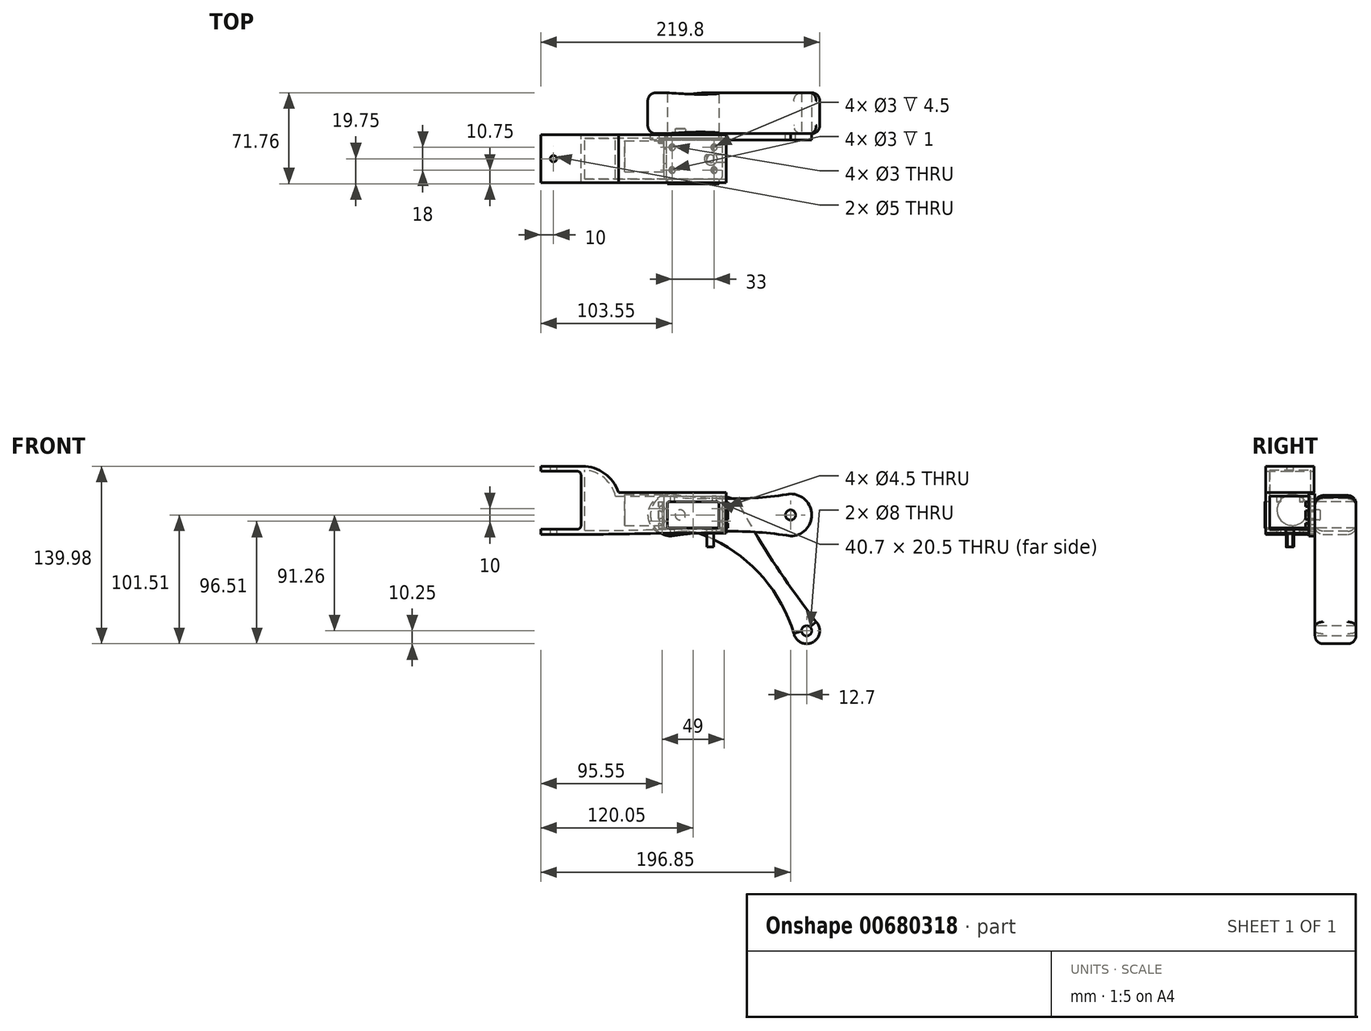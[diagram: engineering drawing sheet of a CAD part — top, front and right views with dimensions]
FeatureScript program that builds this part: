
annotation { "Feature Type Name" : "Feature", "Feature Type Description" : "" }
export const myFeature = defineFeature(function(context is Context, id is Id, definition is map)
    precondition{}
    {
        {
            var Q0;
            Q0=qCreatedBy(makeId("Top.planeOp"),FACE);
            var sketch = newSketch(context, id + "F0", { "sketchPlane" : qUnion([Q0])});
            skLineSegment(sketch, "E0.bottom", {"start": v(-20.35, 19.75) * mm, "end": v(20.35, 19.75) * mm});
            skLineSegment(sketch, "E0.top", {"start": v(-20.35, -19.75) * mm, "end": v(20.35, -19.75) * mm});
            skLineSegment(sketch, "E0.left", {"start": v(-20.35, 19.75) * mm, "end": v(-20.35, -19.75) * mm});
            skLineSegment(sketch, "E0.right", {"start": v(20.35, 19.75) * mm, "end": v(20.35, -19.75) * mm});
            skPoint(sketch, "E1", {"position": v(-20.35, 0) * mm});
            skPoint(sketch, "E2", {"position": v(0, 19.75) * mm});
            skLineSegment(sketch, "E3.bottom", {"start": v(-27.25, 14.75) * mm, "end": v(27.25, 14.75) * mm});
            skLineSegment(sketch, "E3.top", {"start": v(-27.25, 12.25) * mm, "end": v(27.25, 12.25) * mm});
            skLineSegment(sketch, "E3.left", {"start": v(-27.25, 14.75) * mm, "end": v(-27.25, 12.25) * mm});
            skLineSegment(sketch, "E3.right", {"start": v(27.25, 14.75) * mm, "end": v(27.25, 12.25) * mm});
            skPoint(sketch, "E4", {"position": v(0, 14.75) * mm});
            skSolve(sketch);
        }
        {
            var Q0;
            Q0 = qSketchRegion(id + "F0", true);
            extrude(context, id + "F1", {"entities" : qUnion([Q0]), "depth" : 20.5 * mm, "offsetDistance" : 25.4 * mm});
        }
        {
            var Q0;
            Q0=makeQuery(id+"F1.opExtrude","SWEPT_FACE",FACE,{"disambiguationData":[OSD([sQuery(id+"F0.wireOp",EDGE,"E0.bottom")])]});
            var sketch = newSketch(context, id + "F2", { "sketchPlane" : qUnion([Q0])});
            skCircle(sketch, "E5", {"center": v(10.1, 10.25) * mm, "radius": 10.25 * mm, "construction": true});
            skLineSegment(sketch, "E6", {"start": v(20.35, 10.25) * mm, "end": v(-20.35, 10.25) * mm, "construction": true});
            skCircle(sketch, "E7", {"center": v(10.1, 10.25) * mm, "radius": 4 * mm});
            skSolve(sketch);
        }
        {
            var Q0;
            Q0 = qSketchRegion(id + "F2", true);
            extrude(context, id + "F3", {"entities" : qUnion([Q0]), "operationType" : NewBodyOperationType.ADD, "depth" : 4 * mm, "offsetDistance" : 25.4 * mm});
        }
        {
            var Q0;
            Q0=makeQuery(id+"F3.opExtrude","CAP_EDGE",EDGE,{"disambiguationData":[OSD([sQuery(id+"F2.wireOp",EDGE,"E7")])],"isStart":false});
            fillet(context, id + "F4", {"entities" : qUnion([Q0]), "radius" : .5 * mm, "tangentPropagation" : true, "allowEdgeOverflow" : false});
        }
        {
            var Q0;
            {var subQ0=sQuery(id+"F0.wireOp",EDGE,"E3.bottom");Q0=makeQuery(id+"F1.opExtrude","SWEPT_FACE",FACE,{"disambiguationData":[OSD([subQ0]),TDD([makeQuery(id+"F0.imprint","IMPRINT",EDGE,{"disambiguationData":[TD([[makeQuery(id+"F0.imprint","INTERSECT",VERTEX,{"derivedFrom":[subQ0,sQuery(id+"F0.wireOp",EDGE,"E3.left")]}),-1.0]])],"derivedFrom":subQ0})])]});}
            var sketch = newSketch(context, id + "F5", { "sketchPlane" : qUnion([Q0])});
            skLineSegment(sketch, "E8", {"start": v(27.25, 10.25) * mm, "end": v(20.35, 10.25) * mm, "construction": true});
            skLineSegment(sketch, "E9", {"start": v(24.5, 0) * mm, "end": v(24.5, 20.5) * mm, "construction": true});
            skCircle(sketch, "E10", {"center": v(24.5, 15.25) * mm, "radius": 2.25 * mm, "construction": true});
            skArc(sketch, "E11.MirrorC", {"start": v(26.18, 3.75) * mm, "mid": v(22.25, 5.25) * mm, "end": v(26.18, 6.75) * mm});
            skLineSegment(sketch, "E12.bottom", {"start": v(27.25, 3.75) * mm, "end": v(26.18, 3.75) * mm});
            skLineSegment(sketch, "E12.top", {"start": v(27.25, 6.75) * mm, "end": v(26.18, 6.75) * mm});
            skLineSegment(sketch, "E12.left", {"start": v(27.25, 3.75) * mm, "end": v(27.25, 6.75) * mm});
            skLineSegment(sketch, "E13", {"start": v(24.5, 5.25) * mm, "end": v(29.17, 5.25) * mm, "construction": true});
            skPoint(sketch, "E14", {"position": v(27.25, 5.25) * mm});
            skLineSegment(sketch, "E15.MirrorCS", {"start": v(27.25, 16.75) * mm, "end": v(26.18, 16.75) * mm});
            skLineSegment(sketch, "E16.MirrorCS", {"start": v(27.25, 13.75) * mm, "end": v(26.18, 13.75) * mm});
            skLineSegment(sketch, "E17.MirrorCS", {"start": v(27.25, 16.75) * mm, "end": v(27.25, 13.75) * mm});
            skArc(sketch, "E18.MirrorCS", {"start": v(26.18, 16.75) * mm, "mid": v(22.25, 15.25) * mm, "end": v(26.18, 13.75) * mm});
            skPoint(sketch, "E19.MirrorP", {"position": v(27.25, 15.25) * mm});
            skLineSegment(sketch, "E20.MirrorCS", {"start": v(-27.25, 13.75) * mm, "end": v(-26.18, 13.75) * mm});
            skLineSegment(sketch, "E21.MirrorCS", {"start": v(-27.25, 3.75) * mm, "end": v(-26.18, 3.75) * mm});
            skLineSegment(sketch, "E22.MirrorCS", {"start": v(-27.25, 6.75) * mm, "end": v(-26.18, 6.75) * mm});
            skLineSegment(sketch, "E23.MirrorCS", {"start": v(-27.25, 16.75) * mm, "end": v(-26.18, 16.75) * mm});
            skLineSegment(sketch, "E24.MirrorCS", {"start": v(-27.25, 3.75) * mm, "end": v(-27.25, 6.75) * mm});
            skLineSegment(sketch, "E25.MirrorCS", {"start": v(-27.25, 16.75) * mm, "end": v(-27.25, 13.75) * mm});
            skPoint(sketch, "E26.MirrorP", {"position": v(-27.25, 5.25) * mm});
            skArc(sketch, "E27.MirrorCS", {"start": v(-26.18, 3.75) * mm, "mid": v(-22.25, 5.25) * mm, "end": v(-26.18, 6.75) * mm});
            skArc(sketch, "E28.MirrorCS", {"start": v(-26.18, 16.75) * mm, "mid": v(-22.25, 15.25) * mm, "end": v(-26.18, 13.75) * mm});
            skCircle(sketch, "E29.MirrorC", {"center": v(-24.5, 15.25) * mm, "radius": 2.25 * mm, "construction": true});
            skPoint(sketch, "E30.MirrorP", {"position": v(-27.25, 15.25) * mm});
            skSolve(sketch);
        }
        {
            var Q0;
            Q0 = qSketchRegion(id + "F5", true);
            var Q1;
            {var subQ0=sQuery(id+"F0.wireOp",EDGE,"E3.top");Q1=makeQuery(id+"F1.opExtrude","SWEPT_FACE",FACE,{"disambiguationData":[OSD([subQ0]),TDD([makeQuery(id+"F0.imprint","IMPRINT",EDGE,{"disambiguationData":[TD([[makeQuery(id+"F0.imprint","INTERSECT",VERTEX,{"derivedFrom":[subQ0,sQuery(id+"F0.wireOp",EDGE,"E3.left")]}),-1.0]])],"derivedFrom":subQ0})])]});}
            extrude(context, id + "F6", {"entities" : qUnion([Q0]), "operationType" : NewBodyOperationType.REMOVE, "endBound" : BoundingType.UP_TO_SURFACE, "oppositeDirection" : true, "depth" : 25.4 * mm, "endBoundEntityFace" : qUnion([Q1]), "offsetDistance" : 25.4 * mm});
        }
        {
            var Q0;
            {var subQ0=sQuery(id+"F0.wireOp",EDGE,"E0.right");Q0=makeQuery(id+"F1.opExtrude","CAP_EDGE",EDGE,{"disambiguationData":[OSD([subQ0]),TDD([makeQuery(id+"F0.imprint","IMPRINT",EDGE,{"disambiguationData":[TD([[makeQuery(id+"F0.imprint","INTERSECT",VERTEX,{"derivedFrom":[sQuery(id+"F0.wireOp",EDGE,"E0.top"),subQ0]}),1.0]])],"derivedFrom":subQ0})])],"isStart":true});}
            var Q1;
            {var subQ0=sQuery(id+"F0.wireOp",EDGE,"E0.right");Q1=makeQuery(id+"F1.opExtrude","CAP_EDGE",EDGE,{"disambiguationData":[OSD([subQ0]),TDD([makeQuery(id+"F0.imprint","IMPRINT",EDGE,{"disambiguationData":[TD([[makeQuery(id+"F0.imprint","INTERSECT",VERTEX,{"derivedFrom":[sQuery(id+"F0.wireOp",EDGE,"E0.top"),subQ0]}),1.0]])],"derivedFrom":subQ0})])],"isStart":false});}
            var Q2;
            {var subQ0=sQuery(id+"F0.wireOp",EDGE,"E0.left");Q2=makeQuery(id+"F1.opExtrude","CAP_EDGE",EDGE,{"disambiguationData":[OSD([subQ0]),TDD([makeQuery(id+"F0.imprint","IMPRINT",EDGE,{"disambiguationData":[TD([[makeQuery(id+"F0.imprint","INTERSECT",VERTEX,{"derivedFrom":[sQuery(id+"F0.wireOp",EDGE,"E0.top"),subQ0]}),1.0]])],"derivedFrom":subQ0})])],"isStart":true});}
            var Q3;
            {var subQ0=sQuery(id+"F0.wireOp",EDGE,"E0.left");Q3=makeQuery(id+"F1.opExtrude","CAP_EDGE",EDGE,{"disambiguationData":[OSD([subQ0]),TDD([makeQuery(id+"F0.imprint","IMPRINT",EDGE,{"disambiguationData":[TD([[makeQuery(id+"F0.imprint","INTERSECT",VERTEX,{"derivedFrom":[sQuery(id+"F0.wireOp",EDGE,"E0.top"),subQ0]}),1.0]])],"derivedFrom":subQ0})])],"isStart":false});}
            var Q4;
            Q4=makeQuery(id+"F1.opExtrude","CAP_EDGE",EDGE,{"disambiguationData":[OSD([sQuery(id+"F0.wireOp",EDGE,"E0.bottom")])],"isStart":false});
            var Q5;
            Q5=makeQuery(id+"F1.opExtrude","SWEPT_EDGE",EDGE,{"disambiguationData":[OSD([sQuery(id+"F0.wireOp",EDGE,"E0.bottom"),sQuery(id+"F0.wireOp",EDGE,"E0.right")])]});
            var Q6;
            Q6=makeQuery(id+"F1.opExtrude","CAP_EDGE",EDGE,{"disambiguationData":[OSD([sQuery(id+"F0.wireOp",EDGE,"E0.bottom")])],"isStart":true});
            var Q7;
            {var subQ0=sQuery(id+"F0.wireOp",EDGE,"E0.right");Q7=makeQuery(id+"F1.opExtrude","CAP_EDGE",EDGE,{"disambiguationData":[OSD([subQ0]),TDD([makeQuery(id+"F0.imprint","IMPRINT",EDGE,{"disambiguationData":[TD([[makeQuery(id+"F0.imprint","INTERSECT",VERTEX,{"derivedFrom":[sQuery(id+"F0.wireOp",EDGE,"E0.bottom"),subQ0]}),-1.0]])],"derivedFrom":subQ0})])],"isStart":true});}
            var Q8;
            {var subQ0=sQuery(id+"F0.wireOp",EDGE,"E0.right");Q8=makeQuery(id+"F1.opExtrude","CAP_EDGE",EDGE,{"disambiguationData":[OSD([subQ0]),TDD([makeQuery(id+"F0.imprint","IMPRINT",EDGE,{"disambiguationData":[TD([[makeQuery(id+"F0.imprint","INTERSECT",VERTEX,{"derivedFrom":[sQuery(id+"F0.wireOp",EDGE,"E0.bottom"),subQ0]}),-1.0]])],"derivedFrom":subQ0})])],"isStart":false});}
            var Q9;
            Q9=makeQuery(id+"F1.opExtrude","SWEPT_EDGE",EDGE,{"disambiguationData":[OSD([sQuery(id+"F0.wireOp",EDGE,"E0.bottom"),sQuery(id+"F0.wireOp",EDGE,"E0.left")])]});
            var Q10;
            {var subQ0=sQuery(id+"F0.wireOp",EDGE,"E0.left");Q10=makeQuery(id+"F1.opExtrude","CAP_EDGE",EDGE,{"disambiguationData":[OSD([subQ0]),TDD([makeQuery(id+"F0.imprint","IMPRINT",EDGE,{"disambiguationData":[TD([[makeQuery(id+"F0.imprint","INTERSECT",VERTEX,{"derivedFrom":[sQuery(id+"F0.wireOp",EDGE,"E0.bottom"),subQ0]}),-1.0]])],"derivedFrom":subQ0})])],"isStart":true});}
            var Q11;
            {var subQ0=sQuery(id+"F0.wireOp",EDGE,"E0.left");Q11=makeQuery(id+"F1.opExtrude","CAP_EDGE",EDGE,{"disambiguationData":[OSD([subQ0]),TDD([makeQuery(id+"F0.imprint","IMPRINT",EDGE,{"disambiguationData":[TD([[makeQuery(id+"F0.imprint","INTERSECT",VERTEX,{"derivedFrom":[sQuery(id+"F0.wireOp",EDGE,"E0.bottom"),subQ0]}),-1.0]])],"derivedFrom":subQ0})])],"isStart":false});}
            fillet(context, id + "F7", {"entities" : qUnion([Q0, Q1, Q2, Q3, Q4, Q5, Q6, Q7, Q8, Q9, Q10, Q11]), "radius" : 1 * mm, "tangentPropagation" : true, "allowEdgeOverflow" : false});
        }
        {
            var Q0;
            Q0=makeQuery(id+"F1.opExtrude","SWEPT_FACE",FACE,{"disambiguationData":[OSD([sQuery(id+"F0.wireOp",EDGE,"E0.bottom")])]});
            var sketch = newSketch(context, id + "F8", { "sketchPlane" : qUnion([Q0])});
            skLineSegment(sketch, "E31.bottom", {"start": v(33.6, -6.35) * mm, "end": v(-93.4, -6.35) * mm, "construction": true});
            skLineSegment(sketch, "E31.top", {"start": v(33.6, 26.85) * mm, "end": v(-93.4, 26.85) * mm, "construction": true});
            skLineSegment(sketch, "E31.left", {"start": v(33.6, -6.35) * mm, "end": v(33.6, 26.85) * mm, "construction": true});
            skLineSegment(sketch, "E31.right", {"start": v(-93.4, -6.35) * mm, "end": v(-93.4, 26.85) * mm, "construction": true});
            skCircle(sketch, "E32", {"center": v(-76.8, 10.25) * mm, "radius": 16.6 * mm, "construction": true});
            skPoint(sketch, "E32.centerSnap0", {"position": v(-93.4, 10.25) * mm});
            skCircle(sketch, "E33", {"center": v(-46.9, 10.25) * mm, "radius": 13.3 * mm, "construction": true});
            skLineSegment(sketch, "E34", {"start": v(-93.4, 10.25) * mm, "end": v(33.6, 10.25) * mm, "construction": true});
            skArc(sketch, "E35", {"start": v(-76.8, 26.85) * mm, "mid": v(-93.4, 10.25) * mm, "end": v(-76.8, -6.35) * mm});
            skArc(sketch, "E36", {"start": v(17, -6.35) * mm, "mid": v(-29.9, -2.58) * mm, "end": v(-76.8, -6.35) * mm});
            skLineSegment(sketch, "E37", {"start": v(-29.9, 26.85) * mm, "end": v(-29.9, -6.35) * mm, "construction": true});
            skPoint(sketch, "E38.MirrorP", {"position": v(33.6, 10.25) * mm});
            skArc(sketch, "E39.MirrorCS", {"start": v(17, 26.85) * mm, "mid": v(33.6, 10.25) * mm, "end": v(17, -6.35) * mm});
            skArc(sketch, "E40.MirrorCS", {"start": v(17, 26.85) * mm, "mid": v(-29.9, 23.08) * mm, "end": v(-76.8, 26.85) * mm});
            skCircle(sketch, "E41", {"center": v(-76.8, 10.25) * mm, "radius": 4 * mm});
            skLineSegment(sketch, "E42.bottom", {"start": v(-20.35, 0) * mm, "end": v(20.35, 0) * mm});
            skLineSegment(sketch, "E42.top", {"start": v(-20.35, 20.5) * mm, "end": v(20.35, 20.5) * mm});
            skLineSegment(sketch, "E42.left", {"start": v(-20.35, 0) * mm, "end": v(-20.35, 20.5) * mm});
            skLineSegment(sketch, "E42.right", {"start": v(20.35, 0) * mm, "end": v(20.35, 20.5) * mm});
            skCircle(sketch, "E43", {"center": v(-24.5, 15.25) * mm, "radius": 2.25 * mm});
            skCircle(sketch, "E44.MirrorC", {"center": v(-24.5, 5.25) * mm, "radius": 2.25 * mm});
            skCircle(sketch, "E45.MirrorC", {"center": v(24.5, 5.25) * mm, "radius": 2.25 * mm});
            skCircle(sketch, "E46.MirrorC", {"center": v(24.5, 15.25) * mm, "radius": 2.25 * mm});
            skSolve(sketch);
        }
        {
            var Q0;
            Q0 = qSketchRegion(id + "F8", true);
            var Q1;
            {var subQ0=sQuery(id+"F0.wireOp",EDGE,"E3.bottom");Q1=makeQuery(id+"F1.opExtrude","SWEPT_FACE",FACE,{"disambiguationData":[OSD([subQ0]),TDD([makeQuery(id+"F0.imprint","IMPRINT",EDGE,{"disambiguationData":[TD([[makeQuery(id+"F0.imprint","INTERSECT",VERTEX,{"derivedFrom":[subQ0,sQuery(id+"F0.wireOp",EDGE,"E3.right")]}),1.0]])],"derivedFrom":subQ0})])]});}
            extrude(context, id + "F9", {"entities" : qUnion([Q0]), "endBound" : BoundingType.UP_TO_SURFACE, "oppositeDirection" : true, "depth" : 43.94 * mm, "endBoundEntityFace" : qUnion([Q1]), "offsetDistance" : 6.35 * mm, "offsetOppositeDirection" : true});
        }
        {
            var Q0;
            Q0=makeQuery(id+"F1.opExtrude","SWEPT_FACE",FACE,{"disambiguationData":[OSD([sQuery(id+"F0.wireOp",EDGE,"E0.bottom")])]});
            var sketch = newSketch(context, id + "F10", { "sketchPlane" : qUnion([Q0])});
            skLineSegment(sketch, "E47.bottom", {"start": v(32.33, -5.08) * mm, "end": v(-32.33, -5.08) * mm, "construction": true});
            skLineSegment(sketch, "E47.top", {"start": v(32.33, 25.58) * mm, "end": v(-32.33, 25.58) * mm, "construction": true});
            skLineSegment(sketch, "E47.left", {"start": v(32.33, -5.08) * mm, "end": v(32.33, 25.58) * mm, "construction": true});
            skLineSegment(sketch, "E47.right", {"start": v(-32.33, -5.08) * mm, "end": v(-32.33, 25.58) * mm, "construction": true});
            skArc(sketch, "E48", {"start": v(-6.93, -5.08) * mm, "mid": v(-52.48, -36.03) * mm, "end": v(-79.67, -83.92) * mm});
            skLineSegment(sketch, "E49.bottom", {"start": v(37.41, -96.34) * mm, "end": v(-102.3, -96.34) * mm, "construction": true});
            skLineSegment(sketch, "E49.top", {"start": v(37.4, 30.66) * mm, "end": v(-102.3, 30.66) * mm, "construction": true});
            skLineSegment(sketch, "E49.left", {"start": v(37.41, -96.34) * mm, "end": v(37.4, 30.66) * mm, "construction": true});
            skLineSegment(sketch, "E49.right", {"start": v(-102.3, -96.34) * mm, "end": v(-102.3, 30.66) * mm, "construction": true});
            skArc(sketch, "E50", {"start": v(-36.58, 17.72) * mm, "mid": v(-65.2, -29.73) * mm, "end": v(-97.57, -74.69) * mm});
            skArc(sketch, "E51", {"start": v(-97.57, -74.69) * mm, "mid": v(-94.2, -90.12) * mm, "end": v(-79.67, -83.92) * mm});
            skArc(sketch, "E52", {"start": v(20.35, -5.08) * mm, "mid": v(35.68, 10.25) * mm, "end": v(20.35, 25.58) * mm});
            skArc(sketch, "E53", {"start": v(20.35, -5.08) * mm, "mid": v(6.71, -2.54) * mm, "end": v(-6.93, -5.08) * mm});
            skArc(sketch, "E54", {"start": v(-23.8, 24.2) * mm, "mid": v(-1.67, 23.1) * mm, "end": v(20.35, 25.58) * mm});
            skPoint(sketch, "E55.visualSharp", {"position": v(-32.33, 25.58) * mm});
            skArc(sketch, "E55.filletArc", {"start": v(-23.8, 24.2) * mm, "mid": v(-31.2, 22.93) * mm, "end": v(-36.58, 17.72) * mm});
            skCircle(sketch, "E56", {"center": v(-89.5, -81.01) * mm, "radius": 4 * mm});
            skLineSegment(sketch, "E57.bottom", {"start": v(20.35, 0) * mm, "end": v(-20.35, 0) * mm});
            skLineSegment(sketch, "E57.top", {"start": v(20.35, 20.5) * mm, "end": v(-20.35, 20.5) * mm});
            skLineSegment(sketch, "E57.left", {"start": v(20.35, 0) * mm, "end": v(20.35, 20.5) * mm});
            skLineSegment(sketch, "E57.right", {"start": v(-20.35, 0) * mm, "end": v(-20.35, 20.5) * mm});
            skSolve(sketch);
        }
        {
            var Q0;
            Q0 = qSketchRegion(id + "F10", true);
            extrude(context, id + "F11", {"entities" : qUnion([Q0]), "depth" : 32.26 * mm, "offsetDistance" : 25.4 * mm});
        }
        {
            var Q0;
            Q0=makeQuery(id+"F11.opExtrude","SWEPT_FACE",FACE,{"disambiguationData":[OSD([sQuery(id+"F10.wireOp",EDGE,"E48")])]});
            var Q1;
            Q1=makeQuery(id+"F11.opExtrude","SWEPT_FACE",FACE,{"disambiguationData":[OSD([sQuery(id+"F10.wireOp",EDGE,"E52")])]});
            fillet(context, id + "F12", {"entities" : qUnion([Q0, Q1]), "radius" : 6.35 * mm, "tangentPropagation" : true, "allowEdgeOverflow" : false});
        }
        {
            var Q0;
            Q0=qCreatedBy(makeId("Top.planeOp"),FACE);
            var sketch = newSketch(context, id + "F13", { "sketchPlane" : qUnion([Q0])});
            skLineSegment(sketch, "E58.bottom", {"start": v(-23, 16) * mm, "end": v(23, 16) * mm});
            skLineSegment(sketch, "E58.top", {"start": v(-23, -16) * mm, "end": v(23, -16) * mm});
            skLineSegment(sketch, "E58.left", {"start": v(-23, 16) * mm, "end": v(-23, -16) * mm});
            skLineSegment(sketch, "E58.right", {"start": v(23, 16) * mm, "end": v(23, -16) * mm});
            skPoint(sketch, "E59", {"position": v(0, 16) * mm});
            skPoint(sketch, "E60", {"position": v(-23, 0) * mm});
            skLineSegment(sketch, "E61", {"start": v(23, 9) * mm, "end": v(-23, 9) * mm, "construction": true});
            skCircle(sketch, "E62", {"center": v(16.5, 9) * mm, "radius": 1.5 * mm});
            skCircle(sketch, "E63.MirrorC", {"center": v(-16.5, 9) * mm, "radius": 1.5 * mm});
            skCircle(sketch, "E64.MirrorC", {"center": v(-16.5, -9) * mm, "radius": 1.5 * mm});
            skCircle(sketch, "E65.MirrorC", {"center": v(16.5, -9) * mm, "radius": 1.5 * mm});
            skSolve(sketch);
        }
        {
            var Q0;
            Q0 = qSketchRegion(id + "F13", true);
            extrude(context, id + "F14", {"entities" : qUnion([Q0]), "depth" : 25 * mm, "offsetDistance" : 25.4 * mm});
        }
        {
            var Q0;
            Q0=makeQuery(id+"F14.opExtrude","CAP_FACE",FACE,{"disambiguationData":[OSD([sQuery(id+"F13.wireOp",EDGE,"E58.bottom"),sQuery(id+"F13.wireOp",EDGE,"E58.top"),sQuery(id+"F13.wireOp",EDGE,"E58.left"),sQuery(id+"F13.wireOp",EDGE,"E58.right"),sQuery(id+"F13.wireOp",EDGE,"E62"),sQuery(id+"F13.wireOp",EDGE,"E63.MirrorC"),sQuery(id+"F13.wireOp",EDGE,"E64.MirrorC"),sQuery(id+"F13.wireOp",EDGE,"E65.MirrorC")])],"isStart":true});
            var sketch = newSketch(context, id + "F15", { "sketchPlane" : qUnion([Q0])});
            skCircle(sketch, "E66", {"center": v(14, 0) * mm, "radius": 5 * mm});
            skSolve(sketch);
        }
        {
            var Q0;
            Q0 = qSketchRegion(id + "F15", true);
            extrude(context, id + "F16", {"entities" : qUnion([Q0]), "operationType" : NewBodyOperationType.ADD, "depth" : 1 * mm, "offsetDistance" : 25.4 * mm});
        }
        {
            var Q0;
            Q0=makeQuery(id+"F16.opExtrude","CAP_FACE",FACE,{"disambiguationData":[OSD([sQuery(id+"F15.wireOp",EDGE,"E66")])],"isStart":false});
            var sketch = newSketch(context, id + "F17", { "sketchPlane" : qUnion([Q0])});
            skArc(sketch, "E67", {"start": v(16.24, 2) * mm, "mid": v(11, 0) * mm, "end": v(16.24, -2) * mm});
            skLineSegment(sketch, "E68", {"start": v(16.24, 2) * mm, "end": v(16.24, -2) * mm});
            skSolve(sketch);
        }
        {
            var Q0;
            Q0=makeQuery(id+"F17.imprint","IMPRINT",FACE,{"disambiguationData":[TD([[makeQuery(id+"F17.imprint","IMPRINT",EDGE,{"derivedFrom":sQuery(id+"F17.wireOp",EDGE,"E67")}),1.0]])]});
            extrude(context, id + "F18", {"entities" : qUnion([Q0]), "operationType" : NewBodyOperationType.ADD, "depth" : 14 * mm, "offsetDistance" : 25.4 * mm});
        }
        {
            var Q0;
            Q0=makeQuery(id+"F14.opExtrude","SWEPT_FACE",FACE,{"disambiguationData":[OSD([sQuery(id+"F13.wireOp",EDGE,"E58.left")])]});
            var sketch = newSketch(context, id + "F19", { "sketchPlane" : qUnion([Q0])});
            skLineSegment(sketch, "E69", {"start": v(-2, 0) * mm, "end": v(-2, 25) * mm, "construction": true});
            skCircle(sketch, "E70", {"center": v(-2, 14.2) * mm, "radius": 12.2 * mm});
            skSolve(sketch);
        }
        {
            var Q0;
            Q0 = qSketchRegion(id + "F19", true);
            extrude(context, id + "F20", {"entities" : qUnion([Q0]), "operationType" : NewBodyOperationType.ADD, "depth" : 30.8 * mm, "offsetDistance" : 25.4 * mm});
        }
        {
            var Q0;
            Q0=makeQuery(id+"F14.opExtrude","SWEPT_EDGE",EDGE,{"disambiguationData":[OSD([sQuery(id+"F13.wireOp",EDGE,"E58.bottom"),sQuery(id+"F13.wireOp",EDGE,"E58.left")])]});
            var Q1;
            Q1=makeQuery(id+"F14.opExtrude","SWEPT_EDGE",EDGE,{"disambiguationData":[OSD([sQuery(id+"F13.wireOp",EDGE,"E58.bottom"),sQuery(id+"F13.wireOp",EDGE,"E58.right")])]});
            var Q2;
            Q2=makeQuery(id+"F14.opExtrude","SWEPT_EDGE",EDGE,{"disambiguationData":[OSD([sQuery(id+"F13.wireOp",EDGE,"E58.top"),sQuery(id+"F13.wireOp",EDGE,"E58.right")])]});
            var Q3;
            Q3=makeQuery(id+"F14.opExtrude","SWEPT_EDGE",EDGE,{"disambiguationData":[OSD([sQuery(id+"F13.wireOp",EDGE,"E58.top"),sQuery(id+"F13.wireOp",EDGE,"E58.left")])]});
            fillet(context, id + "F21", {"entities" : qUnion([Q0, Q1, Q2, Q3]), "radius" : 2 * mm, "tangentPropagation" : true, "allowEdgeOverflow" : false});
        }
        {
            var Q0;
            Q0=makeQuery(id+"F14.opExtrude","CAP_FACE",FACE,{"disambiguationData":[OSD([sQuery(id+"F13.wireOp",EDGE,"E58.bottom"),sQuery(id+"F13.wireOp",EDGE,"E58.top"),sQuery(id+"F13.wireOp",EDGE,"E58.left"),sQuery(id+"F13.wireOp",EDGE,"E58.right"),sQuery(id+"F13.wireOp",EDGE,"E62"),sQuery(id+"F13.wireOp",EDGE,"E63.MirrorC"),sQuery(id+"F13.wireOp",EDGE,"E64.MirrorC"),sQuery(id+"F13.wireOp",EDGE,"E65.MirrorC")])],"isStart":true});
            var sketch = newSketch(context, id + "F22", { "sketchPlane" : qUnion([Q0])});
            skCircle(sketch, "E71", {"center": v(-16.5, -9) * mm, "radius": 2.5 * mm});
            skCircle(sketch, "E72.MirrorC", {"center": v(-16.5, 9) * mm, "radius": 2.5 * mm});
            skCircle(sketch, "E73.MirrorC", {"center": v(16.5, -9) * mm, "radius": 2.5 * mm});
            skCircle(sketch, "E74.MirrorC", {"center": v(16.5, 9) * mm, "radius": 2.5 * mm});
            skCircle(sketch, "E75", {"center": v(-16.5, -9) * mm, "radius": 1.5 * mm});
            skCircle(sketch, "E76.MirrorC", {"center": v(-16.5, 9) * mm, "radius": 1.5 * mm});
            skCircle(sketch, "E77.MirrorC", {"center": v(16.5, 9) * mm, "radius": 1.5 * mm});
            skCircle(sketch, "E78.MirrorC", {"center": v(16.5, -9) * mm, "radius": 1.5 * mm});
            skSolve(sketch);
        }
        {
            var Q0;
            Q0 = qSketchRegion(id + "F22", true);
            extrude(context, id + "F23", {"entities" : qUnion([Q0]), "operationType" : NewBodyOperationType.ADD, "depth" : 1 * mm, "offsetDistance" : 25.4 * mm});
        }
        {
            var Q0;
            Q0=makeQuery(id+"F23.opExtrude","CAP_EDGE",EDGE,{"disambiguationData":[OSD([sQuery(id+"F22.wireOp",EDGE,"E73.MirrorC")])],"isStart":false});
            var Q1;
            Q1=makeQuery(id+"F23.opExtrude","CAP_EDGE",EDGE,{"disambiguationData":[OSD([sQuery(id+"F22.wireOp",EDGE,"E74.MirrorC")])],"isStart":false});
            var Q2;
            Q2=makeQuery(id+"F23.opExtrude","CAP_EDGE",EDGE,{"disambiguationData":[OSD([sQuery(id+"F22.wireOp",EDGE,"E72.MirrorC")])],"isStart":false});
            var Q3;
            Q3=makeQuery(id+"F23.opExtrude","CAP_EDGE",EDGE,{"disambiguationData":[OSD([sQuery(id+"F22.wireOp",EDGE,"E71")])],"isStart":false});
            fillet(context, id + "F24", {"entities" : qUnion([Q0, Q1, Q2, Q3]), "radius" : .5 * mm, "tangentPropagation" : true, "allowEdgeOverflow" : false});
        }
        {
            var Q0;
            Q0=makeQuery(id+"F14.opExtrude","CAP_EDGE",EDGE,{"disambiguationData":[OSD([sQuery(id+"F13.wireOp",EDGE,"E58.bottom")])],"isStart":true});
            var Q1;
            Q1=makeQuery(id+"F14.opExtrude","CAP_EDGE",EDGE,{"disambiguationData":[OSD([sQuery(id+"F13.wireOp",EDGE,"E58.bottom")])],"isStart":false});
            fillet(context, id + "F25", {"entities" : qUnion([Q0, Q1]), "radius" : 1 * mm, "tangentPropagation" : true, "allowEdgeOverflow" : false});
        }
        {
            var Q0;
            Q0=makeQuery(id+"F14.opExtrude","SWEPT_FACE",FACE,{"disambiguationData":[OSD([sQuery(id+"F13.wireOp",EDGE,"E58.bottom")])]});
            var sketch = newSketch(context, id + "F26", { "sketchPlane" : qUnion([Q0])});
            skLineSegment(sketch, "E79.bottom", {"start": v(-26, 28) * mm, "end": v(58.8, 28) * mm});
            skLineSegment(sketch, "E79.left", {"start": v(-26, 28) * mm, "end": v(-26, -4) * mm});
            skLineSegment(sketch, "E79.right", {"start": v(58.8, 28) * mm, "end": v(58.8, -4) * mm, "construction": true});
            skLineSegment(sketch, "E80", {"start": v(88.3, 44.72) * mm, "end": v(88.3, -1) * mm, "construction": true});
            skLineSegment(sketch, "E81", {"start": v(58.8, 21.86) * mm, "end": v(113.47, 21.86) * mm, "construction": true});
            skPoint(sketch, "E82", {"position": v(88.3, 21.86) * mm});
            skLineSegment(sketch, "E83", {"start": v(21, 2.27) * mm, "end": v(21, -4) * mm, "construction": true});
            skLineSegment(sketch, "E84", {"start": v(-26, -4) * mm, "end": v(21, -4) * mm});
            skLineSegment(sketch, "E85", {"start": v(21, -4) * mm, "end": v(58.8, -4) * mm, "construction": true});
            skLineSegment(sketch, "E86", {"start": v(88.3, 44.72) * mm, "end": v(120.05, 44.72) * mm});
            skLineSegment(sketch, "E87", {"start": v(88.3, -1) * mm, "end": v(120.05, -1) * mm});
            skLineSegment(sketch, "E88", {"start": v(120.05, 44.72) * mm, "end": v(120.05, -1) * mm, "construction": true});
            skLineSegment(sketch, "E89", {"start": v(120.05, 44.72) * mm, "end": v(120.05, 48.72) * mm});
            skLineSegment(sketch, "E90", {"start": v(120.05, 48.72) * mm, "end": v(87.3, 48.72) * mm});
            skLineSegment(sketch, "E91.MirrorCS", {"start": v(120.05, -5) * mm, "end": v(87.3, -5) * mm});
            skLineSegment(sketch, "E92.MirrorCS", {"start": v(120.05, -1) * mm, "end": v(120.05, -5) * mm});
            skArc(sketch, "E93", {"start": v(87.3, 48.72) * mm, "mid": v(69.68, 43) * mm, "end": v(58.8, 28) * mm});
            skArc(sketch, "E94", {"start": v(21, -4) * mm, "mid": v(54.15, -4.75) * mm, "end": v(87.3, -5) * mm});
            skLineSegment(sketch, "E95", {"start": v(88.3, 44.72) * mm, "end": v(88.3, -1) * mm});
            skSolve(sketch);
        }
        {
            var Q0;
            Q0 = qSketchRegion(id + "F26", true);
            var Q1;
            Q1=makeQuery(id+"F14.opExtrude","SWEPT_FACE",FACE,{"disambiguationData":[OSD([sQuery(id+"F13.wireOp",EDGE,"E58.top")])]});
            extrude(context, id + "F27", {"entities" : qUnion([Q0]), "endBound" : BoundingType.UP_TO_SURFACE, "oppositeDirection" : true, "depth" : 29.2 * mm, "endBoundEntityFace" : qUnion([Q1]), "hasOffset" : true, "offsetDistance" : 3 * mm, "offsetOppositeDirection" : true, "hasSecondDirection" : true, "secondDirectionOppositeDirection" : false, "secondDirectionDepth" : 3 * mm});
        }
        {
            var Q0;
            Q0=makeQuery(id+"F27.opExtrude","SWEPT_FACE",FACE,{"disambiguationData":[OSD([sQuery(id+"F26.wireOp",EDGE,"E79.left")])]});
            shell(context, id + "F28", {"entities" : qUnion([Q0]), "thickness" : 3 * mm});
        }
        {
            var Q0;
            Q0=makeQuery(id+"F27.opExtrude","SWEPT_FACE",FACE,{"disambiguationData":[OSD([sQuery(id+"F26.wireOp",EDGE,"E84")])]});
            var sketch = newSketch(context, id + "F29", { "sketchPlane" : qUnion([Q0])});
            skLineSegment(sketch, "E96.bottom", {"start": v(26, -3.13) * mm, "end": v(10.5, -3.13) * mm});
            skLineSegment(sketch, "E96.top", {"start": v(26, 3.12) * mm, "end": v(10.5, 3.12) * mm});
            skLineSegment(sketch, "E96.left", {"start": v(26, -3.12) * mm, "end": v(26, 3.12) * mm});
            skLineSegment(sketch, "E96.right", {"start": v(10.5, -3.12) * mm, "end": v(10.5, 3.12) * mm});
            skPoint(sketch, "E97", {"position": v(10.5, 0) * mm});
            skSolve(sketch);
        }
        {
            var Q0;
            Q0 = qSketchRegion(id + "F29", true);
            var Q1;
            Q1=makeQuery(id+"F28.opShell","OFFSET_FACE",FACE,{"disambiguationData":[OSD([sQuery(id+"F26.wireOp",EDGE,"E84")])]});
            extrude(context, id + "F30", {"entities" : qUnion([Q0]), "operationType" : NewBodyOperationType.REMOVE, "endBound" : BoundingType.UP_TO_SURFACE, "oppositeDirection" : true, "depth" : 25.4 * mm, "endBoundEntityFace" : qUnion([Q1]), "offsetDistance" : 25.4 * mm});
        }
        {
            var Q0;
            Q0=makeQuery(id+"F27.opExtrude","SWEPT_FACE",FACE,{"disambiguationData":[OSD([sQuery(id+"F26.wireOp",EDGE,"E91.MirrorCS")])]});
            var sketch = newSketch(context, id + "F31", { "sketchPlane" : qUnion([Q0])});
            skLineSegment(sketch, "E98", {"start": v(-120.05, 0) * mm, "end": v(-87.3, 0) * mm, "construction": true});
            skCircle(sketch, "E99", {"center": v(-110.05, 0) * mm, "radius": 2.5 * mm});
            skSolve(sketch);
        }
        {
            var Q0;
            Q0 = qSketchRegion(id + "F31", true);
            var Q1;
            Q1=makeQuery(id+"F27.opExtrude","SWEPT_FACE",FACE,{"disambiguationData":[OSD([sQuery(id+"F26.wireOp",EDGE,"E90")])]});
            extrude(context, id + "F32", {"entities" : qUnion([Q0]), "operationType" : NewBodyOperationType.REMOVE, "endBound" : BoundingType.UP_TO_SURFACE, "oppositeDirection" : true, "depth" : 25.4 * mm, "endBoundEntityFace" : qUnion([Q1]), "offsetDistance" : 25.4 * mm});
        }
        {
            var Q0;
            Q0=makeQuery(id+"F27.opExtrude","SWEPT_EDGE",EDGE,{"disambiguationData":[OSD([sQuery(id+"F26.wireOp",EDGE,"E86"),sQuery(id+"F26.wireOp",EDGE,"E95")])]});
            var Q1;
            Q1=makeQuery(id+"F27.opExtrude","SWEPT_EDGE",EDGE,{"disambiguationData":[OSD([sQuery(id+"F26.wireOp",EDGE,"E87"),sQuery(id+"F26.wireOp",EDGE,"E95")])]});
            fillet(context, id + "F33", {"entities" : qUnion([Q0, Q1]), "radius" : 3 * mm, "tangentPropagation" : true, "allowEdgeOverflow" : false});
        }
        {
            var Q0;
            Q0=makeQuery(id+"F27.opExtrude","SWEPT_FACE",FACE,{"disambiguationData":[OSD([sQuery(id+"F26.wireOp",EDGE,"E84")])]});
            var sketch = newSketch(context, id + "F34", { "sketchPlane" : qUnion([Q0])});
            skCircle(sketch, "E100", {"center": v(16.5, -9) * mm, "radius": 1.5 * mm});
            skCircle(sketch, "E101.MirrorC", {"center": v(-16.5, -9) * mm, "radius": 1.5 * mm});
            skCircle(sketch, "E102.MirrorC", {"center": v(-16.5, 9) * mm, "radius": 1.5 * mm});
            skCircle(sketch, "E103.MirrorC", {"center": v(16.5, 9) * mm, "radius": 1.5 * mm});
            skSolve(sketch);
        }
        {
            var Q0;
            Q0 = qSketchRegion(id + "F34", true);
            var Q1;
            Q1=makeQuery(id+"F28.opShell","OFFSET_FACE",FACE,{"disambiguationData":[OSD([sQuery(id+"F26.wireOp",EDGE,"E84")])]});
            extrude(context, id + "F35", {"entities" : qUnion([Q0]), "operationType" : NewBodyOperationType.REMOVE, "endBound" : BoundingType.UP_TO_SURFACE, "oppositeDirection" : true, "depth" : 25.4 * mm, "endBoundEntityFace" : qUnion([Q1]), "offsetDistance" : 25.4 * mm});
        }
    });
